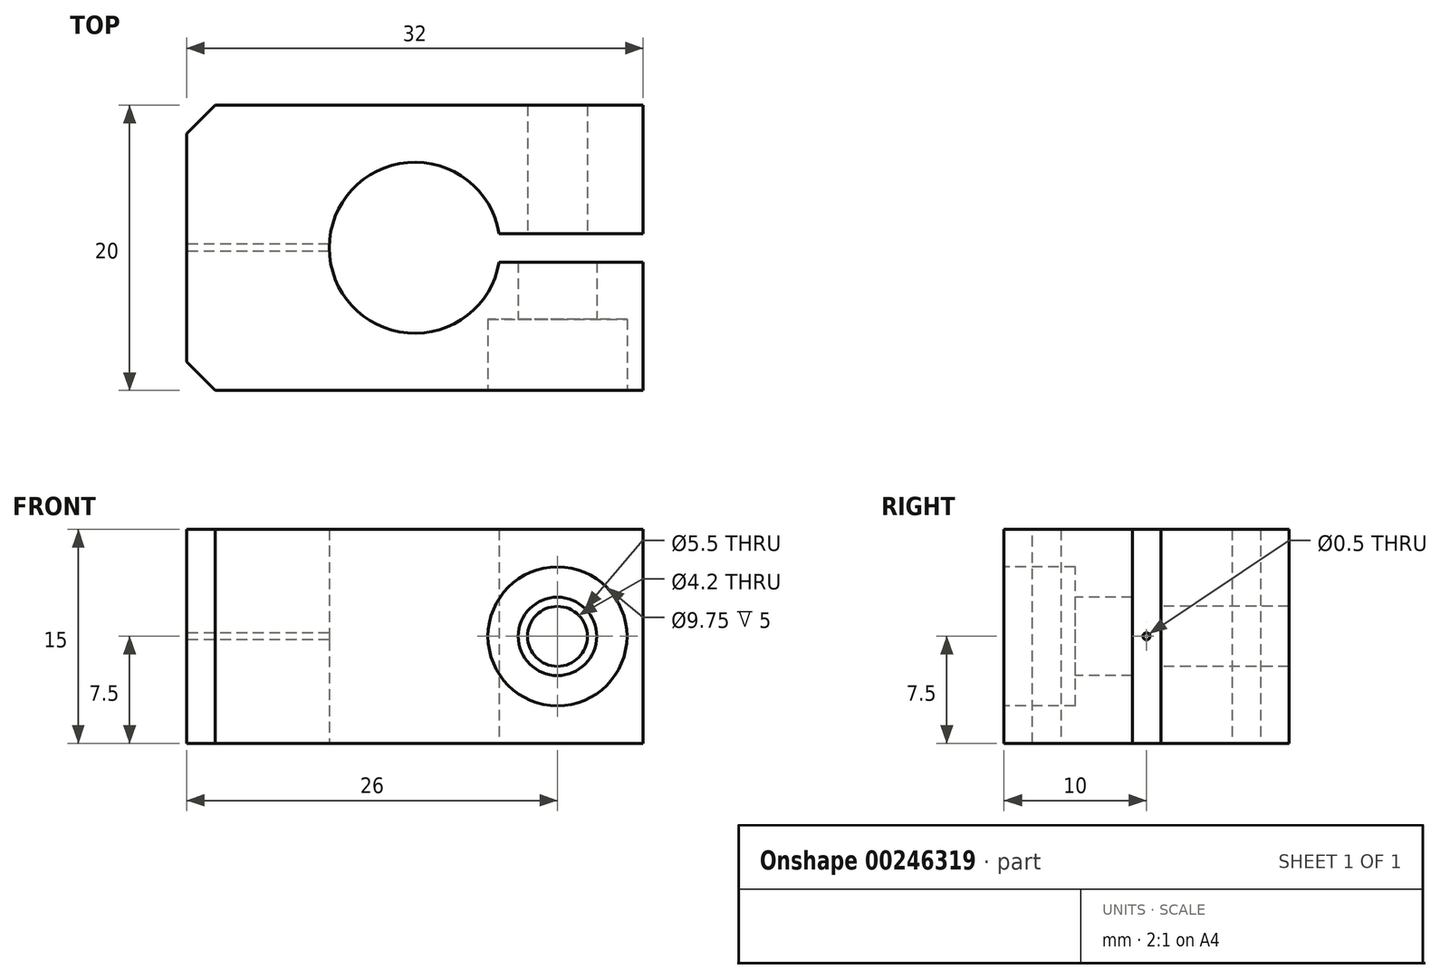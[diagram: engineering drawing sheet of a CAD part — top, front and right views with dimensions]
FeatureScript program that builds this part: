
annotation { "Feature Type Name" : "Feature", "Feature Type Description" : "" }
export const myFeature = defineFeature(function(context is Context, id is Id, definition is map)
    precondition{}
    {
        {
            var Q0;
            Q0=qCreatedBy(makeId("Top.planeOp"),FACE);
            var sketch = newSketch(context, id + "F0", { "sketchPlane" : qUnion([Q0])});
            skArc(sketch, "E0", {"start": v(5.92, 1) * mm, "mid": v(-6, 0) * mm, "end": v(5.92, -1) * mm});
            skLineSegment(sketch, "E1.bottom", {"start": v(-16, 10) * mm, "end": v(16, 10) * mm});
            skLineSegment(sketch, "E1.top", {"start": v(-16, -10) * mm, "end": v(16, -10) * mm});
            skLineSegment(sketch, "E1.left", {"start": v(-16, 10) * mm, "end": v(-16, -10) * mm});
            skLineSegment(sketch, "E1.right", {"start": v(16, 10) * mm, "end": v(16, 1) * mm});
            skLineSegment(sketch, "E2", {"start": v(5.92, 1) * mm, "end": v(16, 1) * mm});
            skLineSegment(sketch, "E3", {"start": v(5.92, -1) * mm, "end": v(16, -1) * mm});
            skLineSegment(sketch, "E4.trimOffspring", {"start": v(16, -1) * mm, "end": v(16, -10) * mm});
            skSolve(sketch);
        }
        {
            var Q0;
            Q0 = qSketchRegion(id + "F0", true);
            extrude(context, id + "F1", {"entities" : qUnion([Q0]), "depth" : 15 * mm});
        }
        {
            var Q0;
            Q0=makeQuery(id+"F1.opExtrude","SWEPT_EDGE",EDGE,{"disambiguationData":[OSD([sQuery(id+"F0.wireOp",EDGE,"E1.bottom"),sQuery(id+"F0.wireOp",EDGE,"E1.left")])]});
            var Q1;
            Q1=makeQuery(id+"F1.opExtrude","SWEPT_EDGE",EDGE,{"disambiguationData":[OSD([sQuery(id+"F0.wireOp",EDGE,"E1.top"),sQuery(id+"F0.wireOp",EDGE,"E1.left")])]});
            chamfer(context, id + "F2", {"entities" : qUnion([Q0, Q1]), "chamferType" : ChamferType.OFFSET_ANGLE, "width" : 2 * mm, "oppositeDirection" : false, "angle" : 45 * degree, "tangentPropagation" : true});
        }
        {
            var Q0;
            Q0=makeQuery(id+"F1.opExtrude","SWEPT_FACE",FACE,{"disambiguationData":[OSD([sQuery(id+"F0.wireOp",EDGE,"E1.top")])]});
            var sketch = newSketch(context, id + "F3", { "sketchPlane" : qUnion([Q0])});
            skPoint(sketch, "E5", {"position": v(10, 7.5) * mm});
            skCircle(sketch, "E6", {"center": v(10, 7.5) * mm, "radius": 2.75 * mm});
            skSolve(sketch);
        }
        {
            var Q0;
            Q0 = qSketchRegion(id + "F3", true);
            extrude(context, id + "F4", {"entities" : qUnion([Q0]), "operationType" : NewBodyOperationType.REMOVE, "oppositeDirection" : true, "depth" : 10 * mm});
        }
        {
            var Q0;
            Q0=makeQuery(id+"F1.opExtrude","SWEPT_FACE",FACE,{"disambiguationData":[OSD([sQuery(id+"F0.wireOp",EDGE,"E1.top")])]});
            var sketch = newSketch(context, id + "F5", { "sketchPlane" : qUnion([Q0])});
            skPoint(sketch, "E7", {"position": v(10, 7.5) * mm});
            skCircle(sketch, "E8", {"center": v(10, 7.5) * mm, "radius": 4.88 * mm});
            skSolve(sketch);
        }
        {
            var Q0;
            Q0=sQuery(id+"F5.wireOp",VERTEX,"E7");
            var Q1;
            Q1=makeQuery(id+"F1.opExtrude","SWEPT_BODY",BODY,{"disambiguationData":[OSD([sQuery(id+"F0.wireOp",EDGE,"E0"),sQuery(id+"F0.wireOp",EDGE,"E1.bottom"),sQuery(id+"F0.wireOp",EDGE,"E1.top"),sQuery(id+"F0.wireOp",EDGE,"E1.left"),sQuery(id+"F0.wireOp",EDGE,"E1.right"),sQuery(id+"F0.wireOp",EDGE,"E2"),sQuery(id+"F0.wireOp",EDGE,"E3"),sQuery(id+"F0.wireOp",EDGE,"E4.trimOffspring")])]});
            hole(context, id + "F6", {"style" : HoleStyle.SIMPLE, "endStyle" : HoleEndStyle.THROUGH, "standardTappedOrClearance" : lookupTablePath({ "standard" : "ISO", "engagement" : "75%", "pitch" : "0.8 mm", "size" : "M5", "type" : "Tapped" }), "standardBlindInLast" : lookupTablePath({ "standard" : "ISO", "engagement" : "75%", "pitch" : "0.8 mm", "size" : "M5", "type" : "Tapped" }), "holeDiameter" : 4.2 * mm, "showTappedDepth" : true, "tappedDepth" : 13 * mm, "tapClearance" : 3, "locations" : qUnion([Q0]), "scope" : qUnion([Q1]), "majorDiameter" : 5 * mm});
        }
        {
            var Q0;
            Q0=makeQuery(id+"F5.imprint","IMPRINT",FACE,{"disambiguationData":[TD([[makeQuery(id+"F5.imprint","IMPRINT",EDGE,{"derivedFrom":sQuery(id+"F5.wireOp",EDGE,"E8")}),1.0]])]});
            extrude(context, id + "F7", {"entities" : qUnion([Q0]), "operationType" : NewBodyOperationType.REMOVE, "oppositeDirection" : true, "depth" : 5 * mm});
        }
        {
            var Q0;
            Q0=makeQuery(id+"F1.opExtrude","SWEPT_FACE",FACE,{"disambiguationData":[OSD([sQuery(id+"F0.wireOp",EDGE,"E1.left")])]});
            var sketch = newSketch(context, id + "F8", { "sketchPlane" : qUnion([Q0])});
            skPoint(sketch, "E9", {"position": v(0, 7.5) * mm});
            skPoint(sketch, "E9.positionSnap0", {"position": v(8, 7.5) * mm});
            skSolve(sketch);
        }
        {
            var Q0;
            Q0=sQuery(id+"F8.wireOp",VERTEX,"E9");
            var Q1;
            Q1=makeQuery(id+"F1.opExtrude","SWEPT_BODY",BODY,{"disambiguationData":[OSD([sQuery(id+"F0.wireOp",EDGE,"E0"),sQuery(id+"F0.wireOp",EDGE,"E1.bottom"),sQuery(id+"F0.wireOp",EDGE,"E1.top"),sQuery(id+"F0.wireOp",EDGE,"E1.left"),sQuery(id+"F0.wireOp",EDGE,"E1.right"),sQuery(id+"F0.wireOp",EDGE,"E2"),sQuery(id+"F0.wireOp",EDGE,"E3"),sQuery(id+"F0.wireOp",EDGE,"E4.trimOffspring")])]});
            hole(context, id + "F9", {"style" : HoleStyle.SIMPLE, "endStyle" : HoleEndStyle.THROUGH, "holeDiameter" : 0.5 * mm, "tappedDepth" : 13 * mm, "tapClearance" : 3, "locations" : qUnion([Q0]), "scope" : qUnion([Q1])});
        }
    });
